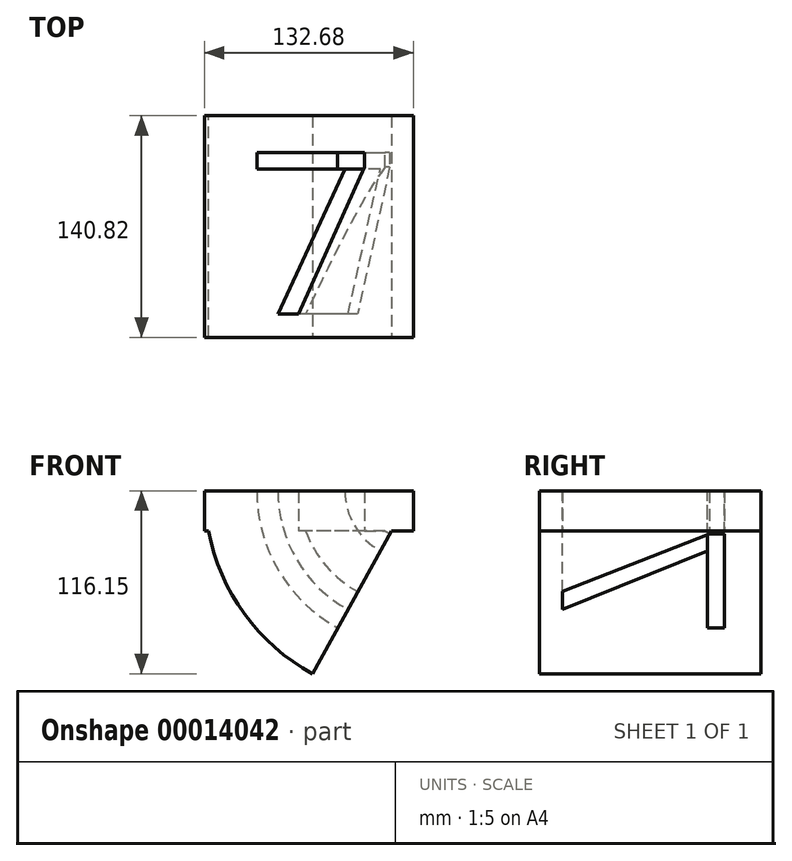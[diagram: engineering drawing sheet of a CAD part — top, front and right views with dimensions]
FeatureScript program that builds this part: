
annotation { "Feature Type Name" : "Feature", "Feature Type Description" : "" }
export const myFeature = defineFeature(function(context is Context, id is Id, definition is map)
    precondition{}
    {
        {
            var Q0;
            Q0=qCreatedBy(makeId("Top.planeOp"),FACE);
            var sketch = newSketch(context, id + "F0", { "sketchPlane" : qUnion([Q0])});
            skLineSegment(sketch, "E0.rect.bottom", {"start": v(66.34, 70.4) * mm, "end": v(-66.34, 70.4) * mm});
            skLineSegment(sketch, "E0.rect.top", {"start": v(66.34, -70.4) * mm, "end": v(-66.34, -70.4) * mm});
            skLineSegment(sketch, "E0.rect.left", {"start": v(66.34, 70.4) * mm, "end": v(66.34, -70.4) * mm});
            skLineSegment(sketch, "E0.rect.right", {"start": v(-66.34, 70.4) * mm, "end": v(-66.34, -70.4) * mm});
            skPoint(sketch, "E0.rect.middle", {"position": v(0, 0) * mm});
            skText(sketch, "E1", { "text": "7", "fontName": "OpenSans-Regular.ttf"});
            const initialGuessF0  = {"E1": [-0.03968, -0.05555, 1, 0, 0.10358]};
            skSetInitialGuess(sketch, initialGuessF0);
            skSolve(sketch);
        }
        {
            var Q0;
            Q0=makeQuery(id+"F0.imprint","IMPRINT",FACE,{"disambiguationData":[TD([[makeQuery(id+"F0.imprint","IMPRINT",EDGE,{"derivedFrom":sQuery(id+"F0.wireOp",EDGE,"E0.rect.bottom")}),1.0]])]});
            extrude(context, id + "F1", {"entities" : qUnion([Q0]), "depth" : 25.4 * mm});
        }
        {
            var Q0;
            Q0=makeQuery(id+"F1.opExtrude","CAP_FACE",FACE,{"disambiguationData":[OSD([sQuery(id+"F0.wireOp",EDGE,"E0.rect.bottom"),sQuery(id+"F0.wireOp",EDGE,"E0.rect.top"),sQuery(id+"F0.wireOp",EDGE,"E0.rect.left"),sQuery(id+"F0.wireOp",EDGE,"E0.rect.right"),sQuery(id+"F0.wireOp",EDGE,"E1.sketch_text.stroke-0"),sQuery(id+"F0.wireOp",EDGE,"E1.sketch_text.stroke-1"),sQuery(id+"F0.wireOp",EDGE,"E1.sketch_text.stroke-2"),sQuery(id+"F0.wireOp",EDGE,"E1.sketch_text.stroke-3"),sQuery(id+"F0.wireOp",EDGE,"E1.sketch_text.stroke-4"),sQuery(id+"F0.wireOp",EDGE,"E1.sketch_text.stroke-5"),sQuery(id+"F0.wireOp",EDGE,"E1.sketch_text.stroke-6")])],"isStart":false});
            var Q1;
            Q1=makeQuery(id+"F1.opExtrude","CAP_EDGE",EDGE,{"disambiguationData":[OSD([sQuery(id+"F0.wireOp",EDGE,"E0.rect.left")])],"isStart":false});
            revolve(context, id + "F2", {"operationType" : NewBodyOperationType.ADD, "entities" : qUnion([Q0]), "axis" : qUnion([Q1]), "revolveType" : RevolveType.ONE_DIRECTION, "angle" : 61.1 * degree});
        }
    });
